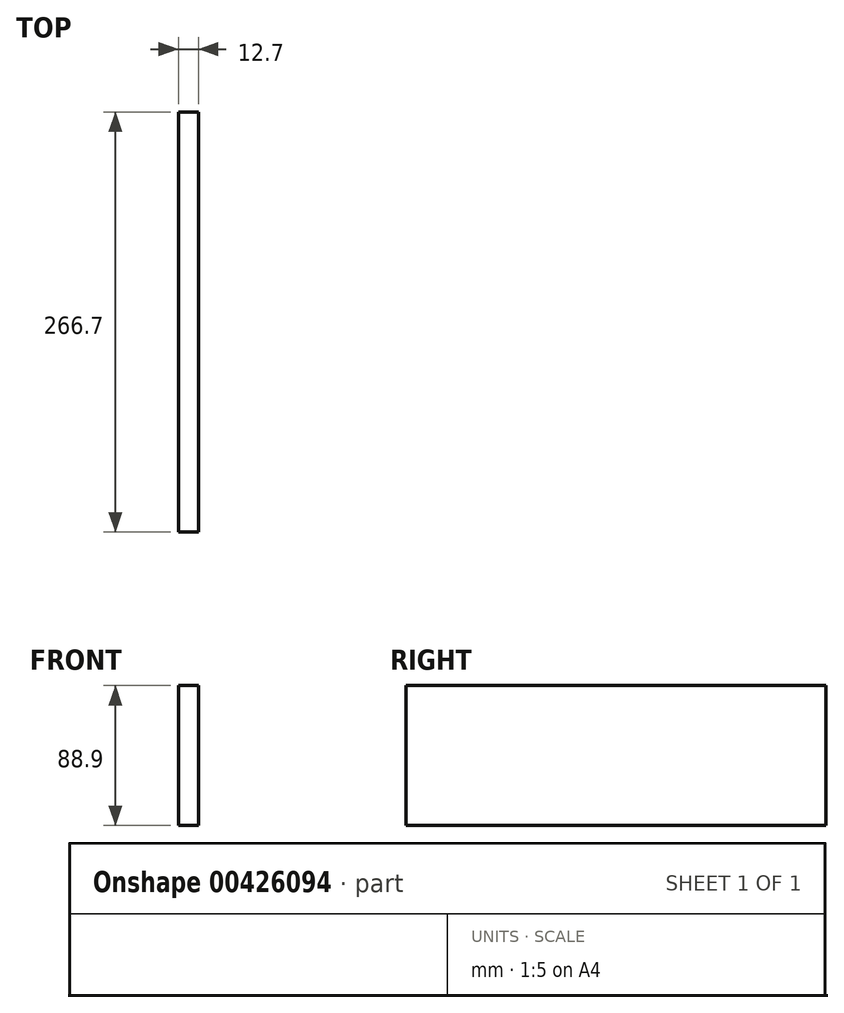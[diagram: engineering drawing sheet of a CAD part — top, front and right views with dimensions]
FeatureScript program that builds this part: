
annotation { "Feature Type Name" : "Feature", "Feature Type Description" : "" }
export const myFeature = defineFeature(function(context is Context, id is Id, definition is map)
    precondition{}
    {
        {
            var Q0;
            Q0=qCreatedBy(makeId("Front.planeOp"),FACE);
            var sketch = newSketch(context, id + "F0", { "sketchPlane" : qUnion([Q0])});
            skLineSegment(sketch, "E0.bottom", {"start": v(6.35, -44.45) * mm, "end": v(-6.35, -44.45) * mm});
            skLineSegment(sketch, "E0.top", {"start": v(6.35, 44.45) * mm, "end": v(-6.35, 44.45) * mm});
            skLineSegment(sketch, "E0.left", {"start": v(6.35, -44.45) * mm, "end": v(6.35, 44.45) * mm});
            skLineSegment(sketch, "E0.right", {"start": v(-6.35, -44.45) * mm, "end": v(-6.35, 44.45) * mm});
            skPoint(sketch, "E0.middle", {"position": v(0, 0) * mm});
            skSolve(sketch);
        }
        {
            var Q0;
            Q0 = qSketchRegion(id + "F0", true);
            extrude(context, id + "F1", {"entities" : qUnion([Q0]), "endBound" : BoundingType.SYMMETRIC, "depth" : 266.7 * mm});
        }
    });
